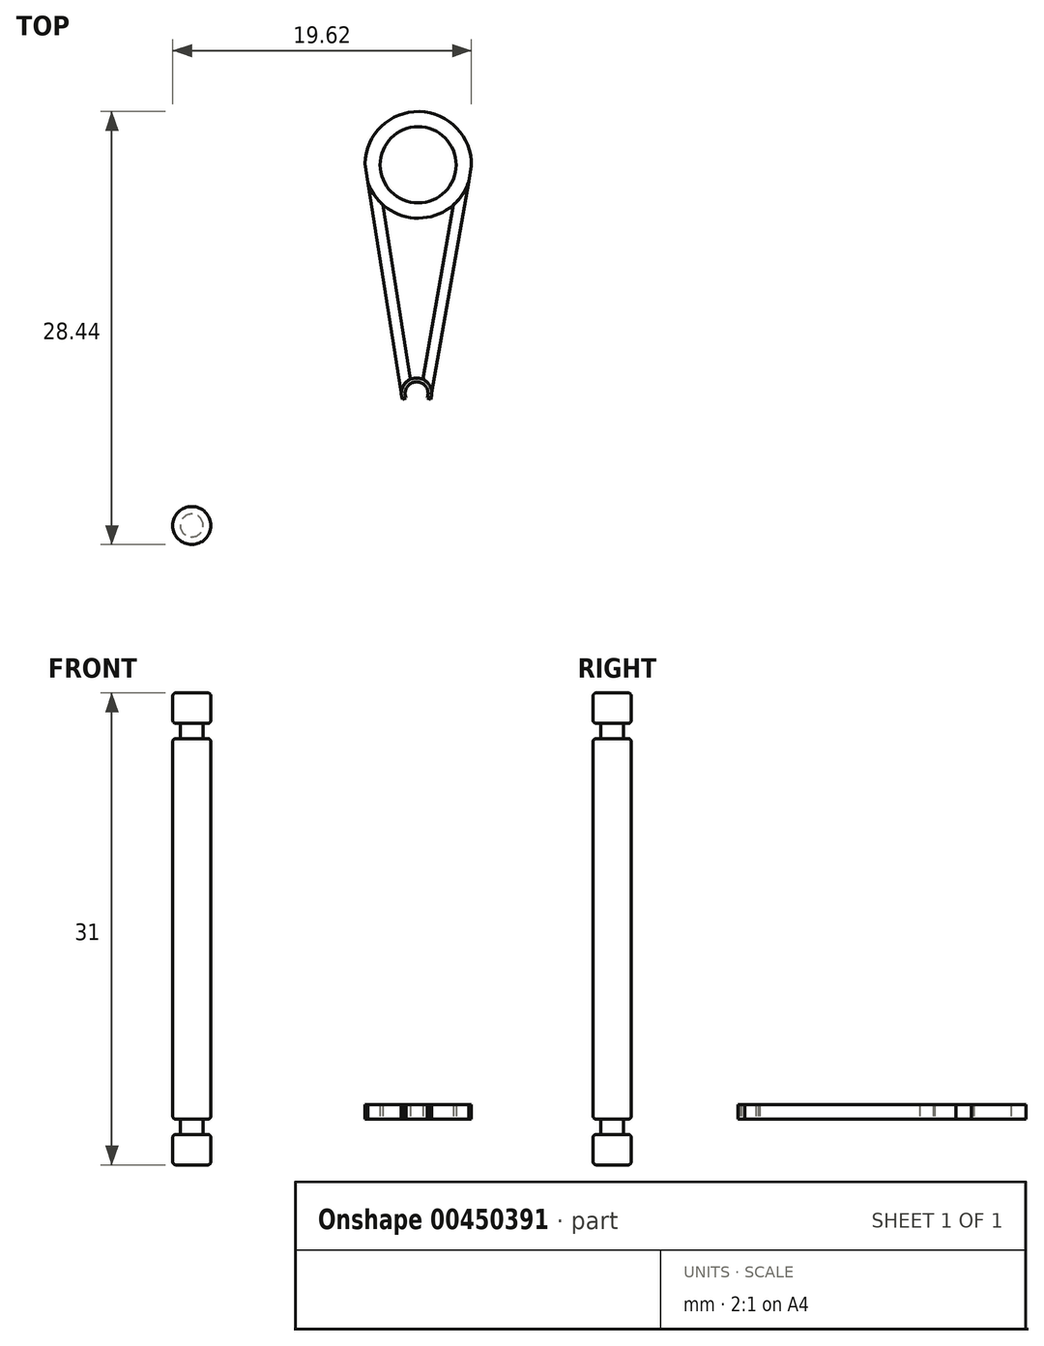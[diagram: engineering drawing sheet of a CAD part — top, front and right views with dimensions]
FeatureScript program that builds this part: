
annotation { "Feature Type Name" : "Feature", "Feature Type Description" : "" }
export const myFeature = defineFeature(function(context is Context, id is Id, definition is map)
    precondition{}
    {
        {
            var Q0;
            Q0=qCreatedBy(makeId("Top.planeOp"),FACE);
            var sketch = newSketch(context, id + "F0", { "sketchPlane" : qUnion([Q0])});
            skCircle(sketch, "E0", {"center": v(-14.05, 1.28) * mm, "radius": 1.25 * mm});
            skSolve(sketch);
        }
        {
            var Q0;
            Q0=makeQuery(id+"F0.imprint","IMPRINT",FACE,{"disambiguationData":[TD([[makeQuery(id+"F0.imprint","IMPRINT",EDGE,{"derivedFrom":sQuery(id+"F0.wireOp",EDGE,"E0")}),1.0]])]});
            extrude(context, id + "F1", {"entities" : qUnion([Q0]), "depth" : 25 * mm});
        }
        {
            var Q0;
            Q0=makeQuery(id+"F1.opExtrude","CAP_FACE",FACE,{"disambiguationData":[OSD([sQuery(id+"F0.wireOp",EDGE,"E0")])],"isStart":false});
            var sketch = newSketch(context, id + "F2", { "sketchPlane" : qUnion([Q0])});
            skCircle(sketch, "E1", {"center": v(-14.05, 1.28) * mm, "radius": 0.75 * mm});
            skSolve(sketch);
        }
        {
            var Q0;
            Q0 = qSketchRegion(id + "F2", true);
            extrude(context, id + "F3", {"entities" : qUnion([Q0]), "operationType" : NewBodyOperationType.ADD, "depth" : 1 * mm});
        }
        {
            var Q0;
            Q0=makeQuery(id+"F3.opExtrude","CAP_FACE",FACE,{"disambiguationData":[OSD([sQuery(id+"F2.wireOp",EDGE,"E1")])],"isStart":false});
            var sketch = newSketch(context, id + "F4", { "sketchPlane" : qUnion([Q0])});
            skCircle(sketch, "E2", {"center": v(-14.05, 1.28) * mm, "radius": 1.25 * mm});
            skSolve(sketch);
        }
        {
            var Q0;
            Q0 = qSketchRegion(id + "F4", true);
            extrude(context, id + "F5", {"entities" : qUnion([Q0]), "operationType" : NewBodyOperationType.ADD, "depth" : 2 * mm});
        }
        {
            var Q0;
            Q0=makeQuery(id+"F1.opExtrude","CAP_EDGE",EDGE,{"disambiguationData":[OSD([sQuery(id+"F0.wireOp",EDGE,"E0")])],"isStart":false});
            var Q1;
            Q1=makeQuery(id+"F5.opExtrude","CAP_EDGE",EDGE,{"disambiguationData":[OSD([sQuery(id+"F4.wireOp",EDGE,"E2")])],"isStart":true});
            var Q2;
            Q2=makeQuery(id+"F5.opExtrude","CAP_EDGE",EDGE,{"disambiguationData":[OSD([sQuery(id+"F4.wireOp",EDGE,"E2")])],"isStart":false});
            var Q3;
            Q3=makeQuery(id+"F1.opExtrude","CAP_EDGE",EDGE,{"disambiguationData":[OSD([sQuery(id+"F0.wireOp",EDGE,"E0")])],"isStart":true});
            fillet(context, id + "F6", {"entities" : qUnion([Q0, Q1, Q2, Q3]), "radius" : .2 * mm, "tangentPropagation" : true, "allowEdgeOverflow" : false});
        }
        {
            var Q0;
            Q0=makeQuery(id+"F1.opExtrude","CAP_FACE",FACE,{"disambiguationData":[OSD([sQuery(id+"F0.wireOp",EDGE,"E0")])],"isStart":true});
            var sketch = newSketch(context, id + "F7", { "sketchPlane" : qUnion([Q0])});
            skCircle(sketch, "E3", {"center": v(-14.05, -1.28) * mm, "radius": 0.75 * mm});
            skSolve(sketch);
        }
        {
            var Q0;
            Q0 = qSketchRegion(id + "F7", true);
            extrude(context, id + "F8", {"entities" : qUnion([Q0]), "operationType" : NewBodyOperationType.ADD, "depth" : 1 * mm});
        }
        {
            var Q0;
            Q0=makeQuery(id+"F8.opExtrude","CAP_FACE",FACE,{"disambiguationData":[OSD([sQuery(id+"F7.wireOp",EDGE,"E3")])],"isStart":false});
            var sketch = newSketch(context, id + "F9", { "sketchPlane" : qUnion([Q0])});
            skCircle(sketch, "E4", {"center": v(-14.05, -1.28) * mm, "radius": 1.25 * mm});
            skSolve(sketch);
        }
        {
            var Q0;
            Q0 = qSketchRegion(id + "F9", true);
            extrude(context, id + "F10", {"entities" : qUnion([Q0]), "operationType" : NewBodyOperationType.ADD, "depth" : 2 * mm});
        }
        {
            var Q0;
            Q0=makeQuery(id+"F10.opExtrude","CAP_EDGE",EDGE,{"disambiguationData":[OSD([sQuery(id+"F9.wireOp",EDGE,"E4")])],"isStart":false});
            var Q1;
            Q1=makeQuery(id+"F10.opExtrude","CAP_EDGE",EDGE,{"disambiguationData":[OSD([sQuery(id+"F9.wireOp",EDGE,"E4")])],"isStart":true});
            fillet(context, id + "F11", {"entities" : qUnion([Q0, Q1]), "radius" : .2 * mm, "tangentPropagation" : true, "allowEdgeOverflow" : false});
        }
        {
            var Q0;
            Q0=qCreatedBy(makeId("Top.planeOp"),FACE);
            var sketch = newSketch(context, id + "F12", { "sketchPlane" : qUnion([Q0])});
            skLineSegment(sketch, "E5", {"start": v(0, 9.75) * mm, "end": v(-0.2, 9.56) * mm, "construction": true});
            skLineSegment(sketch, "E6", {"start": v(1.44, 9.75) * mm, "end": v(1.63, 9.56) * mm, "construction": true});
            skArc(sketch, "E7", {"start": v(1.44, 9.75) * mm, "mid": v(0.72, 10.72) * mm, "end": v(0, 9.75) * mm});
            skLineSegment(sketch, "E8", {"start": v(0, 9.75) * mm, "end": v(-0.2, 9.56) * mm});
            skLineSegment(sketch, "E9", {"start": v(1.44, 9.75) * mm, "end": v(1.63, 9.56) * mm});
            skArc(sketch, "E10", {"start": v(1.63, 9.56) * mm, "mid": v(0.72, 10.97) * mm, "end": v(-0.2, 9.56) * mm});
            skSolve(sketch);
        }
        {
            var Q0;
            Q0=makeQuery(id+"F12.imprint","IMPRINT",FACE,{"disambiguationData":[TD([[makeQuery(id+"F12.imprint","IMPRINT",EDGE,{"derivedFrom":sQuery(id+"F12.wireOp",EDGE,"E7")}),-1.0]])]});
            var sketch = newSketch(context, id + "F13", { "sketchPlane" : qUnion([Q0])});
            skLineSegment(sketch, "E11", {"start": v(-2.68, 25.05) * mm, "end": v(4.32, 24.89) * mm, "construction": true});
            skCircle(sketch, "E12", {"center": v(0.82, 24.97) * mm, "radius": 3.5 * mm});
            skCircle(sketch, "E13", {"center": v(0.82, 24.97) * mm, "radius": 2.5 * mm});
            skLineSegment(sketch, "E14", {"start": v(-2.68, 25.05) * mm, "end": v(-0.28, 10) * mm});
            skLineSegment(sketch, "E15", {"start": v(-1.5, 22.36) * mm, "end": v(0.32, 10.88) * mm});
            skLineSegment(sketch, "E16", {"start": v(4.32, 24.89) * mm, "end": v(1.72, 10) * mm});
            skLineSegment(sketch, "E17", {"start": v(3.15, 22.36) * mm, "end": v(1.12, 10.88) * mm});
            skCircle(sketch, "E18", {"center": v(0.72, 9.98) * mm, "radius": 0.75 * mm, "construction": true});
            skLineSegment(sketch, "E19", {"start": v(-0.2, 9.56) * mm, "end": v(0.03, 9.67) * mm});
            skLineSegment(sketch, "E20", {"start": v(1.63, 9.56) * mm, "end": v(1.4, 9.67) * mm});
            skLineSegment(sketch, "E21", {"start": v(0.03, 9.67) * mm, "end": v(0, 9.75) * mm});
            skLineSegment(sketch, "E22", {"start": v(1.4, 9.67) * mm, "end": v(1.44, 9.75) * mm});
            skSolve(sketch);
        }
        {
            var Q0;
            {var subQ0=sQuery(id+"F13.wireOp",EDGE,"cXiUr87O-DA5x-epRi-p0KX-j3B1mTfHVkrI");Q0=makeQuery(id+"F13.imprint","IMPRINT",FACE,{"disambiguationData":[TD([[makeQuery(id+"F13.imprint","IMPRINT",EDGE,{"derivedFrom":subQ0}),-1.0]])]});}
            var Q1;
            {var subQ0=sQuery(id+"F13.wireOp",EDGE,"OQHTb0HT-Is9h-IgCy-8xdz-5aDt3xUuE5hA");Q1=makeQuery(id+"F13.imprint","IMPRINT",FACE,{"disambiguationData":[TD([[makeQuery(id+"F13.imprint","IMPRINT",EDGE,{"derivedFrom":subQ0}),1.0]])]});}
            var Q2;
            Q2=makeQuery(id+"F12.imprint","IMPRINT",FACE,{"disambiguationData":[TD([[makeQuery(id+"F12.imprint","IMPRINT",EDGE,{"derivedFrom":sQuery(id+"F12.wireOp",EDGE,"E7")}),-1.0]])]});
            var Q3;
            Q3=makeQuery(id+"F13.imprint","IMPRINT",FACE,{"disambiguationData":[TD([[makeQuery(id+"F13.imprint","IMPRINT",EDGE,{"derivedFrom":sQuery(id+"F13.wireOp",EDGE,"E13")}),-1.0]])]});
            var Q4;
            Q4=makeQuery(id+"F13.imprint","IMPRINT",FACE,{"disambiguationData":[TD([[makeQuery(id+"F13.imprint","IMPRINT",EDGE,{"derivedFrom":sQuery(id+"F13.wireOp",EDGE,"E19")}),1.0]])]});
            var Q5;
            Q5=makeQuery(id+"F13.imprint","IMPRINT",FACE,{"disambiguationData":[TD([[makeQuery(id+"F13.imprint","IMPRINT",EDGE,{"derivedFrom":sQuery(id+"F13.wireOp",EDGE,"E20")}),-1.0]])]});
            extrude(context, id + "F14", {"entities" : qUnion([Q0, Q1, Q2, Q3, Q4, Q5]), "depth" : .95 * mm});
        }
        {
            var Q0;
            {var subQ0=sQuery(id+"F13.wireOp",EDGE,"E15");Q0=makeQuery(id+"F13.imprint","IMPRINT",FACE,{"disambiguationData":[TD([[makeQuery(id+"F13.imprint","IMPRINT",EDGE,{"derivedFrom":subQ0}),-1.0]])]});}
            var Q1;
            {var subQ0=sQuery(id+"F13.wireOp",EDGE,"E17");Q1=makeQuery(id+"F13.imprint","IMPRINT",FACE,{"disambiguationData":[TD([[makeQuery(id+"F13.imprint","IMPRINT",EDGE,{"derivedFrom":subQ0}),1.0]])]});}
            extrude(context, id + "F15", {"entities" : qUnion([Q0, Q1]), "depth" : .95 * mm});
        }
    });
